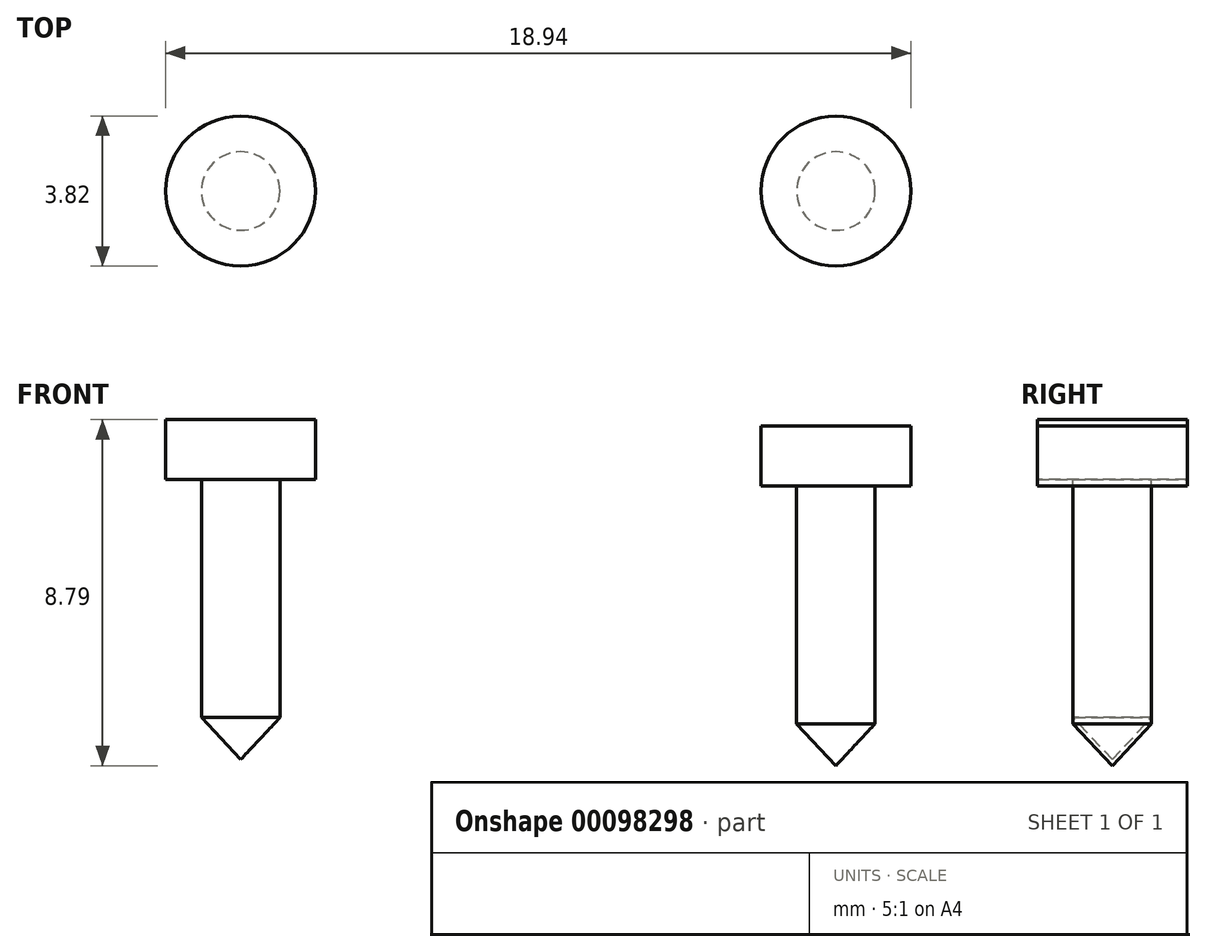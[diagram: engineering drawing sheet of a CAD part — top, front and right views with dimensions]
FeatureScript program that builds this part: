
annotation { "Feature Type Name" : "Feature", "Feature Type Description" : "" }
export const myFeature = defineFeature(function(context is Context, id is Id, definition is map)
    precondition{}
    {
        {
            var Q0;
            Q0=qCreatedBy(makeId("Front.planeOp"),FACE);
            var sketch = newSketch(context, id + "F0", { "sketchPlane" : qUnion([Q0])});
            skLineSegment(sketch, "E0", {"start": v(0, 0) * mm, "end": v(1, 1.07) * mm});
            skLineSegment(sketch, "E1", {"start": v(1, 1.07) * mm, "end": v(1, 7.11) * mm});
            skLineSegment(sketch, "E2", {"start": v(1, 7.11) * mm, "end": v(1.9, 7.11) * mm});
            skLineSegment(sketch, "E3", {"start": v(1.9, 7.11) * mm, "end": v(1.9, 8.64) * mm});
            skLineSegment(sketch, "E4", {"start": v(1.9, 8.64) * mm, "end": v(0, 8.64) * mm});
            skLineSegment(sketch, "E5", {"start": v(0, 8.64) * mm, "end": v(0, 0) * mm});
            skSolve(sketch);
        }
        {
            var Q0;
            Q0=qSketchRegion(id+"F0",true);
            var Q1;
            Q1=sQuery(id+"F0.wireOp",EDGE,"E5");
            revolve(context, id + "F1", {"entities" : qUnion([Q0]), "axis" : qUnion([Q1]), "revolveType" : RevolveType.FULL});
        }
        {
            var Q0;
            Q0=qCreatedBy(makeId("Front.planeOp"),FACE);
            var sketch = newSketch(context, id + "F2", { "sketchPlane" : qUnion([Q0])});
            skLineSegment(sketch, "E6", {"start": v(-15.12, 0.15) * mm, "end": v(-14.12, 1.22) * mm});
            skLineSegment(sketch, "E7", {"start": v(-14.12, 1.22) * mm, "end": v(-14.12, 7.27) * mm});
            skLineSegment(sketch, "E8", {"start": v(-14.12, 7.27) * mm, "end": v(-13.22, 7.27) * mm});
            skLineSegment(sketch, "E9", {"start": v(-13.22, 7.27) * mm, "end": v(-13.22, 8.8) * mm});
            skLineSegment(sketch, "E10", {"start": v(-13.22, 8.8) * mm, "end": v(-15.12, 8.8) * mm});
            skLineSegment(sketch, "E11", {"start": v(-15.12, 8.8) * mm, "end": v(-15.12, 0.15) * mm});
            skSolve(sketch);
        }
        {
            var Q0;
            Q0=makeQuery(id+"F2.imprint","IMPRINT",FACE,{"disambiguationData":[TD([[makeQuery(id+"F2.imprint","IMPRINT",EDGE,{"derivedFrom":sQuery(id+"F2.wireOp",EDGE,"E6")}),1.0]])]});
            var Q1;
            Q1=sQuery(id+"F2.wireOp",EDGE,"E11");
            revolve(context, id + "F3", {"entities" : qUnion([Q0]), "axis" : qUnion([Q1]), "revolveType" : RevolveType.FULL});
        }
    });
